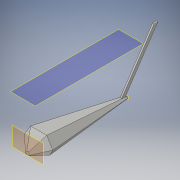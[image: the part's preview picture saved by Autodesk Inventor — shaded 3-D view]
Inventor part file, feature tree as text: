
AUTODESK INVENTOR PART (.ipt)
format: ipt  version: 2016 (Build 200138000, 138)  size: 144,384 bytes
history: native  units: in
note: dims shown in document units (in); Inventor stores cm internally (conversion verified against a paired STEP export)
features: sketch x5, plane x3, loft x3
ambient origin geometry x8: Origin, YZ Plane, XZ Plane, XY Plane, X Axis, Y Axis, Z Axis, Center Point
bodies: Solid1 (feature_tree)
feature tree (11):
  sketch  "Sketch1"  dims[d0=-12.0in d1=1.5in]
  plane  "Work Plane1"
  sketch  "Sketch2"  dims[d2=0.0in d3=90.0deg d4=0.0in d5=90.0deg]
  plane  "Work Plane2"
  loft  "Loft1"
  loft  "Loft2"
  sketch  "Sketch4"  dims[d10=-7.0in]
  plane  "Work Plane3"
  loft  "Loft3"
  sketch  "Sketch3"  dims[d6=0.0in d7=90.0deg d8=0.0in d9=90.0deg]
  sketch  "Sketch5"  dims[d11=0.0in d12=90.0deg d13=0.0in d14=90.0deg]
